# Revit family: 3437A_HCS_PHDIM_Dimmingz-zconverter
name_source: partatom
category: Communication Devices
revit_build: Autodesk Revit 2014 (Build: 20130308_1515(x64)
units: mm (PartAtom-declared; Revit-internal decimal feet)

## types (1)
- 3437A_HCS_PHDIM_Dimmingz-zconverter
    Assembly Code = D5090
    Certification = ETL / cETL Damp Locations
UL 2043, Suitable for Use in Air Handling Spaces (Plenum Rated)
RoHS compliant
    Default Elevation = 48 "
    Description = The PHDIM-1277 converter connects to the dimming device using the familiar purple and grey low voltage dimming wires. The output of the PHDIM1277 tracks the low voltage control input and provides a linear line voltage AC phase control output.
    Features = Standard 0 – 10V dimming input
Dims standard 120 or 277 volts lighting loads
Automatic voltage detection
Compatible with Electronic Low Voltage loads
Mounts to J-box with 1/2” nipple
Plenum rated housing
Suitable for damp locations
5 year warranty
ETL, cETL Listed
RoHs compiant
    Housing Material = Paint - Hubbell - Carbon Black
    L = 5.3 "
    Manufacturer = Hubbell Control Solutions
    Model = PHDIM-1277
    Product Documentation Link = https://hubbellcdn.com
    Product Page URL = https://www.hubbell.com
    Type Comments = Power Packs and Relays
    URL = https://www.hubbell.com
    Warranty = 5-Years Warranty
    Washer = Metal-Hubbell-Galvanized_Steel

## geometry (parser evidence)
native form markers: Sweep x1
no freeform markers — native parametric forms only
